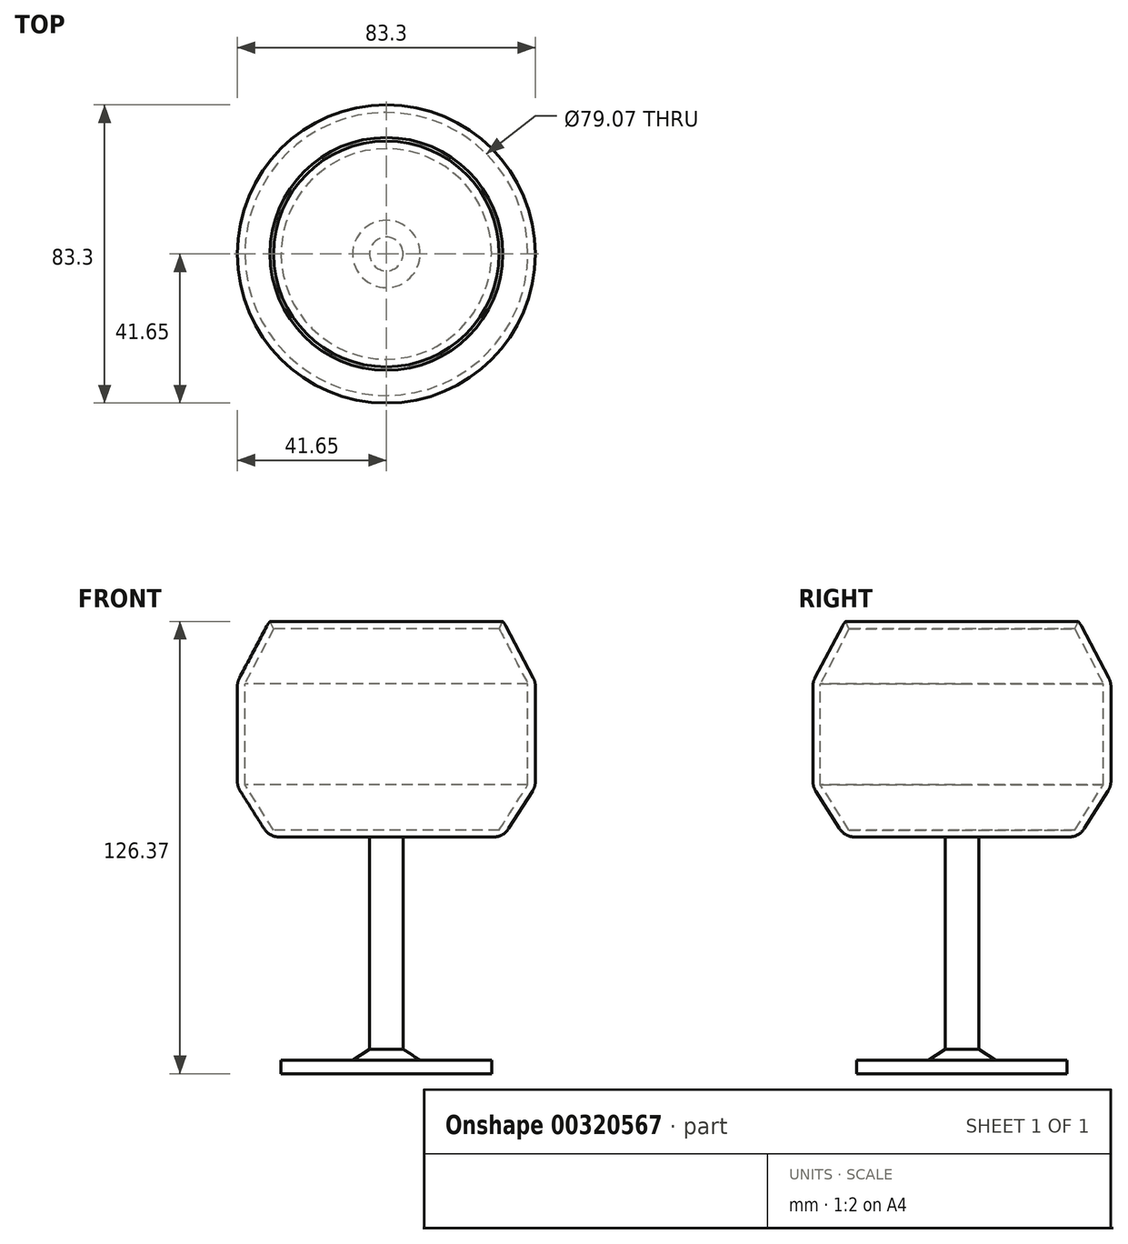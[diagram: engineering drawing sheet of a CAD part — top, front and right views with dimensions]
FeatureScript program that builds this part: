
annotation { "Feature Type Name" : "Feature", "Feature Type Description" : "" }
export const myFeature = defineFeature(function(context is Context, id is Id, definition is map)
    precondition{}
    {
        {
            var Q0;
            Q0=qCreatedBy(makeId("Front.planeOp"),FACE);
            var sketch = newSketch(context, id + "F0", { "sketchPlane" : qUnion([Q0])});
            skLineSegment(sketch, "E0", {"start": v(-32.51, 53.89) * mm, "end": v(-32.7, 53.89) * mm});
            skLineSegment(sketch, "E1", {"start": v(-32.7, 53.89) * mm, "end": v(-41.65, 36.95) * mm});
            skLineSegment(sketch, "E2", {"start": v(-41.65, 36.95) * mm, "end": v(-41.65, 7.77) * mm});
            skLineSegment(sketch, "E3", {"start": v(-41.65, 7.77) * mm, "end": v(-32.7, -6.35) * mm});
            skLineSegment(sketch, "E4", {"start": v(-32.7, -6.35) * mm, "end": v(-12.7, -6.35) * mm});
            skLineSegment(sketch, "E5", {"start": v(-4.7, -6.35) * mm, "end": v(-4.7, -65.66) * mm});
            skLineSegment(sketch, "E6", {"start": v(-4.7, -65.66) * mm, "end": v(-9.41, -68.71) * mm});
            skLineSegment(sketch, "E7", {"start": v(-9.41, -68.71) * mm, "end": v(-29.42, -68.71) * mm});
            skLineSegment(sketch, "E8", {"start": v(-29.42, -68.71) * mm, "end": v(-29.42, -72.48) * mm});
            skLineSegment(sketch, "E9", {"start": v(-29.42, -72.48) * mm, "end": v(0, -72.48) * mm});
            skLineSegment(sketch, "E10", {"start": v(-12.7, -6.35) * mm, "end": v(-4.7, -6.35) * mm});
            skLineSegment(sketch, "E11", {"start": v(-31.53, 51.77) * mm, "end": v(-31.53, 51.77) * mm});
            skLineSegment(sketch, "E12", {"start": v(-31.53, 51.77) * mm, "end": v(-39.53, 36.48) * mm});
            skLineSegment(sketch, "E13", {"start": v(-39.53, 36.48) * mm, "end": v(-39.53, 8.24) * mm});
            skLineSegment(sketch, "E14", {"start": v(-39.53, 8.24) * mm, "end": v(-31.53, -4.4) * mm});
            skLineSegment(sketch, "E15", {"start": v(-31.53, -4.4) * mm, "end": v(-12.47, -4.4) * mm});
            skLineSegment(sketch, "E16", {"start": v(-12.47, -4.4) * mm, "end": v(0, -4.4) * mm});
            skLineSegment(sketch, "E17", {"start": v(-32.51, 53.89) * mm, "end": v(-31.53, 51.77) * mm});
            skPoint(sketch, "E18.orphan", {"position": v(0, 53.89) * mm});
            skPoint(sketch, "E19.orphan", {"position": v(0, 51.77) * mm});
            skLineSegment(sketch, "E20", {"start": v(0, 75.3) * mm, "end": v(0, -76) * mm});
            skSolve(sketch);
        }
        {
            var Q0;
            Q0=makeQuery(id+"F0.imprint","IMPRINT",FACE,{"disambiguationData":[TD([[makeQuery(id+"F0.imprint","IMPRINT",EDGE,{"derivedFrom":sQuery(id+"F0.wireOp",EDGE,"E0")}),1.0]])]});
            var Q1;
            Q1=sQuery(id+"F0.wireOp",EDGE,"E20");
            revolve(context, id + "F1", {"entities" : qUnion([Q0]), "axis" : qUnion([Q1]), "revolveType" : RevolveType.FULL});
        }
        {
            var Q0;
            Q0=makeQuery(id+"F1.opRevolve","SWEPT_EDGE",EDGE,{"disambiguationData":[OSD([sQuery(id+"F0.wireOp",EDGE,"E0"),sQuery(id+"F0.wireOp",EDGE,"E1")])]});
            fillet(context, id + "F2", {"entities" : qUnion([Q0]), "radius" : 7.62 * mm, "tangentPropagation" : true, "allowEdgeOverflow" : false});
        }
        {
            var Q0;
            Q0=makeQuery(id+"F1.opRevolve","SWEPT_EDGE",EDGE,{"disambiguationData":[OSD([sQuery(id+"F0.wireOp",EDGE,"E1"),sQuery(id+"F0.wireOp",EDGE,"E2")])]});
            fillet(context, id + "F3", {"entities" : qUnion([Q0]), "radius" : 5.08 * mm, "tangentPropagation" : true, "allowEdgeOverflow" : false});
        }
        {
            var Q0;
            Q0=makeQuery(id+"F1.opRevolve","SWEPT_EDGE",EDGE,{"disambiguationData":[OSD([sQuery(id+"F0.wireOp",EDGE,"E2"),sQuery(id+"F0.wireOp",EDGE,"E3")])]});
            fillet(context, id + "F4", {"entities" : qUnion([Q0]), "radius" : 5.08 * mm, "tangentPropagation" : true, "allowEdgeOverflow" : false});
        }
        {
            var Q0;
            Q0=makeQuery(id+"F1.opRevolve","SWEPT_EDGE",EDGE,{"disambiguationData":[OSD([sQuery(id+"F0.wireOp",EDGE,"E3"),sQuery(id+"F0.wireOp",EDGE,"E4")])]});
            fillet(context, id + "F5", {"entities" : qUnion([Q0]), "radius" : 5.08 * mm, "tangentPropagation" : true, "allowEdgeOverflow" : false});
        }
    });
